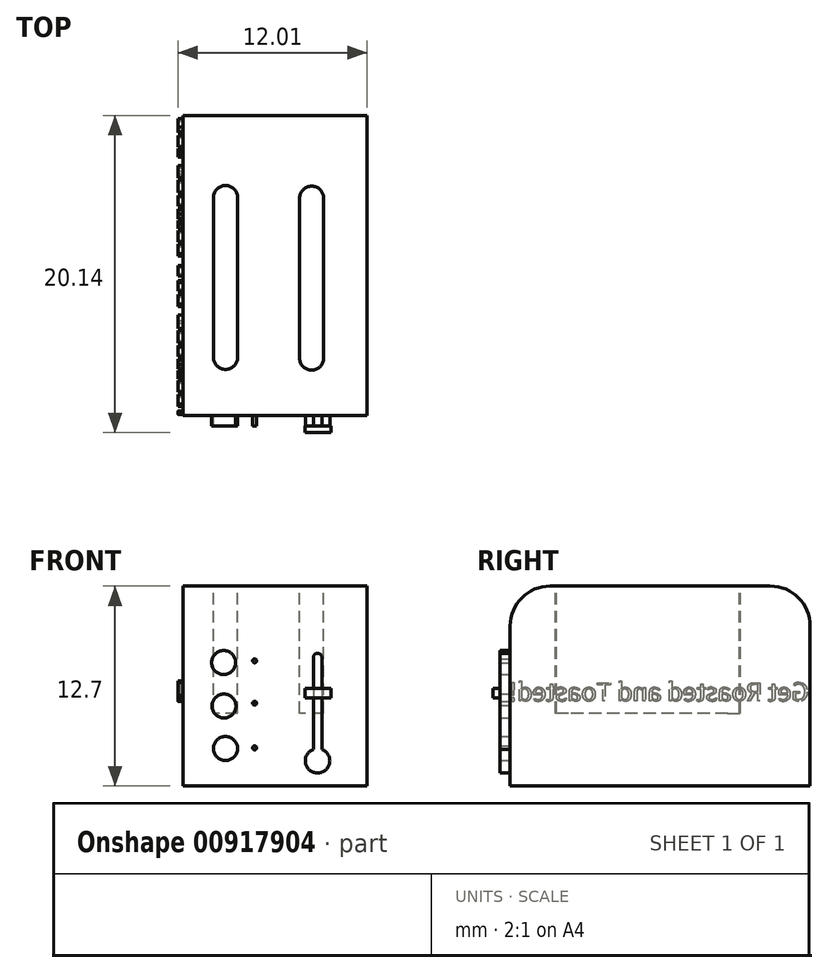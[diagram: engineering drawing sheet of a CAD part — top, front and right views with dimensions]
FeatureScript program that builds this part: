
annotation { "Feature Type Name" : "Feature", "Feature Type Description" : "" }
export const myFeature = defineFeature(function(context is Context, id is Id, definition is map)
    precondition{}
    {
        {
            var Q0;
            Q0=qCreatedBy(makeId("Right.planeOp"),FACE);
            var sketch = newSketch(context, id + "F0", { "sketchPlane" : qUnion([Q0])});
            skLineSegment(sketch, "E0.bottom", {"start": v(-12.32, 5.78) * mm, "end": v(1.65, 5.78) * mm});
            skLineSegment(sketch, "E0.top", {"start": v(-14.86, -6.92) * mm, "end": v(4.19, -6.92) * mm});
            skLineSegment(sketch, "E0.left", {"start": v(-14.86, 3.24) * mm, "end": v(-14.86, -6.92) * mm});
            skLineSegment(sketch, "E0.right", {"start": v(4.19, 3.24) * mm, "end": v(4.19, -6.92) * mm});
            skPoint(sketch, "E1.visualSharp", {"position": v(4.19, 5.78) * mm});
            skArc(sketch, "E1.filletArc", {"start": v(4.19, 3.24) * mm, "mid": v(3.44, 5.04) * mm, "end": v(1.65, 5.78) * mm});
            skPoint(sketch, "E2.visualSharp", {"position": v(-14.86, 5.78) * mm});
            skArc(sketch, "E2.filletArc", {"start": v(-12.32, 5.78) * mm, "mid": v(-14.12, 5.04) * mm, "end": v(-14.86, 3.24) * mm});
            skSolve(sketch);
        }
        {
            var Q0;
            Q0 = qSketchRegion(id + "F0", true);
            extrude(context, id + "F1", {"entities" : qUnion([Q0]), "depth" : 11.68 * mm, "offsetDistance" : 25.4 * mm});
        }
        {
            var Q0;
            Q0=makeQuery(id+"F1.opExtrude","SWEPT_FACE",FACE,{"disambiguationData":[OSD([sQuery(id+"F0.wireOp",EDGE,"E0.bottom")])]});
            var sketch = newSketch(context, id + "F2", { "sketchPlane" : qUnion([Q0])});
            skLineSegment(sketch, "E3.bottom", {"start": v(2.43, -1.02) * mm, "end": v(3.45, -1.02) * mm});
            skLineSegment(sketch, "E3.top", {"start": v(1.93, -11.18) * mm, "end": v(3.45, -11.18) * mm});
            skLineSegment(sketch, "E3.left", {"start": v(1.93, -1.53) * mm, "end": v(1.93, -11.18) * mm});
            skLineSegment(sketch, "E3.right", {"start": v(3.45, -1.02) * mm, "end": v(3.45, -11.18) * mm});
            skLineSegment(sketch, "E4.bottom", {"start": v(7.4, -1.06) * mm, "end": v(8.92, -1.06) * mm});
            skLineSegment(sketch, "E4.top", {"start": v(7.4, -11.22) * mm, "end": v(8.92, -11.22) * mm});
            skLineSegment(sketch, "E4.left", {"start": v(7.4, -1.06) * mm, "end": v(7.4, -11.22) * mm});
            skLineSegment(sketch, "E4.right", {"start": v(8.92, -1.06) * mm, "end": v(8.92, -11.22) * mm});
            skPoint(sketch, "E5.visualSharp", {"position": v(1.93, -1.02) * mm});
            skArc(sketch, "E6", {"start": v(3.45, -1.02) * mm, "mid": v(2.69, -0.26) * mm, "end": v(1.93, -1.02) * mm});
            skArc(sketch, "E7", {"start": v(1.93, -11.18) * mm, "mid": v(2.69, -11.94) * mm, "end": v(3.45, -11.18) * mm});
            skArc(sketch, "E8", {"start": v(8.92, -1.06) * mm, "mid": v(8.16, -0.3) * mm, "end": v(7.4, -1.06) * mm});
            skArc(sketch, "E9", {"start": v(7.4, -11.22) * mm, "mid": v(8.16, -11.99) * mm, "end": v(8.92, -11.22) * mm});
            skLineSegment(sketch, "E10", {"start": v(1.93, -1.53) * mm, "end": v(1.93, -1.02) * mm});
            skLineSegment(sketch, "E11", {"start": v(1.93, -1.02) * mm, "end": v(2.43, -1.02) * mm});
            skSolve(sketch);
        }
        {
            var Q0;
            Q0 = qSketchRegion(id + "F2", true);
            extrude(context, id + "F3", {"entities" : qUnion([Q0]), "operationType" : NewBodyOperationType.REMOVE, "oppositeDirection" : true, "depth" : 8.08 * mm, "offsetDistance" : 25.4 * mm});
        }
        {
            var Q0;
            Q0=makeQuery(id+"F1.opExtrude","SWEPT_FACE",FACE,{"disambiguationData":[OSD([sQuery(id+"F0.wireOp",EDGE,"E0.left")])]});
            var sketch = newSketch(context, id + "F4", { "sketchPlane" : qUnion([Q0])});
            skCircle(sketch, "E12", {"center": v(2.57, 0.92) * mm, "radius": 0.76 * mm});
            skCircle(sketch, "E13", {"center": v(2.6, -1.84) * mm, "radius": 0.76 * mm});
            skPoint(sketch, "E13.centerSnap0", {"position": v(0, -1.84) * mm});
            skCircle(sketch, "E14", {"center": v(2.68, -4.54) * mm, "radius": 0.77 * mm});
            skCircle(sketch, "E15", {"center": v(4.54, 1.04) * mm, "radius": 0.13 * mm});
            skCircle(sketch, "E16", {"center": v(4.54, -1.66) * mm, "radius": 0.13 * mm});
            skCircle(sketch, "E17", {"center": v(4.54, -4.5) * mm, "radius": 0.13 * mm});
            skLineSegment(sketch, "E18.bottom", {"start": v(8.26, 1.25) * mm, "end": v(8.8, 1.25) * mm});
            skLineSegment(sketch, "E18.top", {"start": v(8.26, -4.59) * mm, "end": v(8.8, -4.59) * mm});
            skLineSegment(sketch, "E18.left", {"start": v(8.26, 1.25) * mm, "end": v(8.26, -4.59) * mm});
            skLineSegment(sketch, "E18.right", {"start": v(8.8, 1.25) * mm, "end": v(8.8, -4.59) * mm});
            skArc(sketch, "E19", {"start": v(8.8, 1.25) * mm, "mid": v(8.53, 1.52) * mm, "end": v(8.26, 1.25) * mm});
            skArc(sketch, "E20", {"start": v(8.26, -4.59) * mm, "mid": v(8.53, -6.1) * mm, "end": v(8.8, -4.59) * mm});
            skSolve(sketch);
        }
        {
            var Q0;
            Q0 = qSketchRegion(id + "F4", true);
            extrude(context, id + "F5", {"entities" : qUnion([Q0]), "operationType" : NewBodyOperationType.ADD, "depth" : 0.66 * mm, "offsetDistance" : 25.4 * mm});
        }
        {
            var Q0;
            Q0=makeQuery(id+"F5.opExtrude","CAP_FACE",FACE,{"disambiguationData":[OSD([sQuery(id+"F4.wireOp",EDGE,"E18.left"),sQuery(id+"F4.wireOp",EDGE,"E18.right"),sQuery(id+"F4.wireOp",EDGE,"E19"),sQuery(id+"F4.wireOp",EDGE,"E20")])],"isStart":false});
            var sketch = newSketch(context, id + "F6", { "sketchPlane" : qUnion([Q0])});
            skLineSegment(sketch, "E21.bottom", {"start": v(7.73, -0.72) * mm, "end": v(9.37, -0.72) * mm});
            skLineSegment(sketch, "E21.top", {"start": v(7.73, -1.33) * mm, "end": v(9.37, -1.33) * mm});
            skLineSegment(sketch, "E21.left", {"start": v(7.73, -0.72) * mm, "end": v(7.73, -1.33) * mm});
            skLineSegment(sketch, "E21.right", {"start": v(9.37, -0.72) * mm, "end": v(9.37, -1.33) * mm});
            skSolve(sketch);
        }
        {
            var Q0;
            Q0 = qSketchRegion(id + "F6", true);
            extrude(context, id + "F7", {"entities" : qUnion([Q0]), "operationType" : NewBodyOperationType.ADD, "depth" : 0.43 * mm, "offsetDistance" : 25.4 * mm});
        }
        {
            var Q0;
            Q0=makeQuery(id+"F1.opExtrude","CAP_FACE",FACE,{"disambiguationData":[OSD([sQuery(id+"F0.wireOp",EDGE,"E0.bottom"),sQuery(id+"F0.wireOp",EDGE,"E0.top"),sQuery(id+"F0.wireOp",EDGE,"E0.left"),sQuery(id+"F0.wireOp",EDGE,"E0.right"),sQuery(id+"F0.wireOp",EDGE,"E1.filletArc"),sQuery(id+"F0.wireOp",EDGE,"E2.filletArc")])],"isStart":true});
            var sketch = newSketch(context, id + "F8", { "sketchPlane" : qUnion([Q0])});
            skText(sketch, "E22", { "text": "Get Roasted and Toasted!", "fontName": "NotoSansCJKtc-Regular.otf"});
            const initialGuessF8  = {"E22": [-0.00409, -0.00152, 1, 0, 0.00114]};
            skSetInitialGuess(sketch, initialGuessF8);
            skSolve(sketch);
        }
        {
            var Q0;
            Q0 = qSketchRegion(id + "F8", true);
            extrude(context, id + "F9", {"entities" : qUnion([Q0]), "operationType" : NewBodyOperationType.ADD, "depth" : 0.33 * mm, "offsetDistance" : 25.4 * mm});
        }
    });
